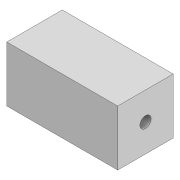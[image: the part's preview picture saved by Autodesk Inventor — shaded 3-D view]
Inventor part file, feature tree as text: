
AUTODESK INVENTOR PART (.ipt)
format: ipt  version: 2021 (Build 250183000, 183)  size: 90,112 bytes
history: native  units: mm
features: sketch x2, extrude x1, hole x1
ambient origin geometry x8: Origin, YZ Plane, XZ Plane, XY Plane, X Axis, Y Axis, Z Axis, Center Point
bodies: Volumenkörper1 (feature_tree)
feature tree (4):
  extrude  "Extrusion1"  Depth=20.0mm
  hole  "Bohrung1"  [1 undecoded]
  sketch  "Skizze1"  dims[d0=40.0mm d1=20.0mm]
  sketch  "Skizze2"  dims[d2=20.0mm d3=0.0mm d4=5.0mm d5=10.0mm d6=10.0mm d7=10.0mm d8=10.0mm d9=4.0mm d10=6.0mm d11=4.0mm d12=2.0mm d13=90.0deg d14=8.0mm d15=20.594885mm]
note: 1 required parameter value undecoded (feature->parameter linkage not recoverable at this tier; creation-order binding heuristic only, values carry confidence <= 0.55)
